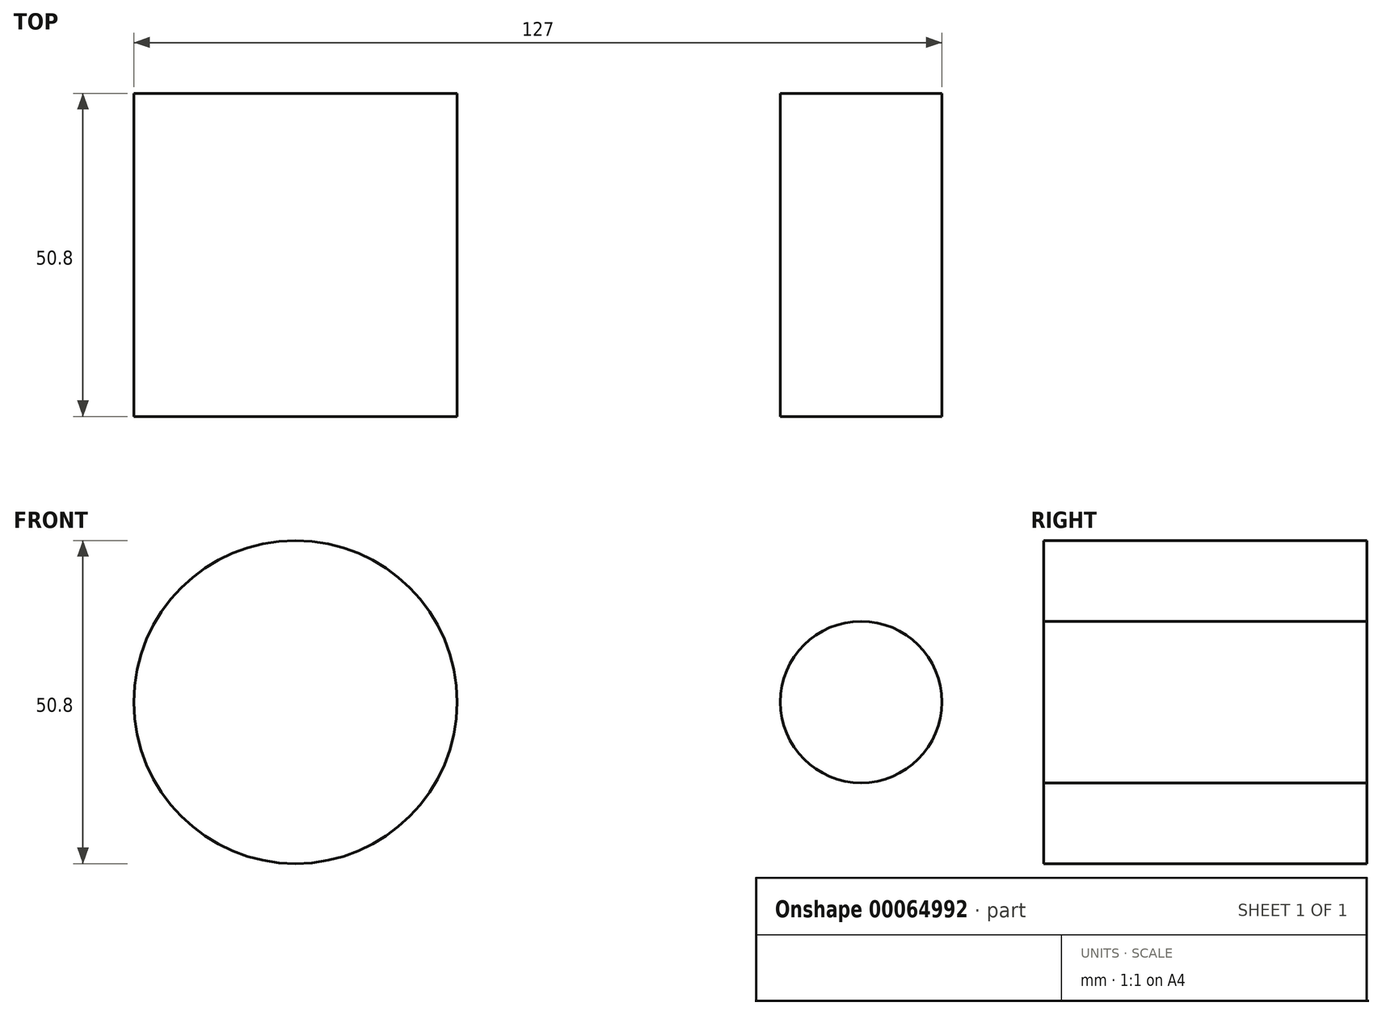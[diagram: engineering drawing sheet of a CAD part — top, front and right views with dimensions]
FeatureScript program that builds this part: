
annotation { "Feature Type Name" : "Feature", "Feature Type Description" : "" }
export const myFeature = defineFeature(function(context is Context, id is Id, definition is map)
    precondition{}
    {
        {
            var Q0;
            Q0=qCreatedBy(makeId("Front.planeOp"),FACE);
            var sketch = newSketch(context, id + "F0", { "sketchPlane" : qUnion([Q0])});
            skCircle(sketch, "E0", {"center": v(0, 0) * mm, "radius": 12.7 * mm});
            skCircle(sketch, "E1", {"center": v(-88.9, 0) * mm, "radius": 25.4 * mm});
            skSolve(sketch);
        }
        {
            var Q0;
            Q0 = qSketchRegion(id + "F0", true);
            extrude(context, id + "F1", {"entities" : qUnion([Q0]), "depth" : 50.8 * mm});
        }
    });
